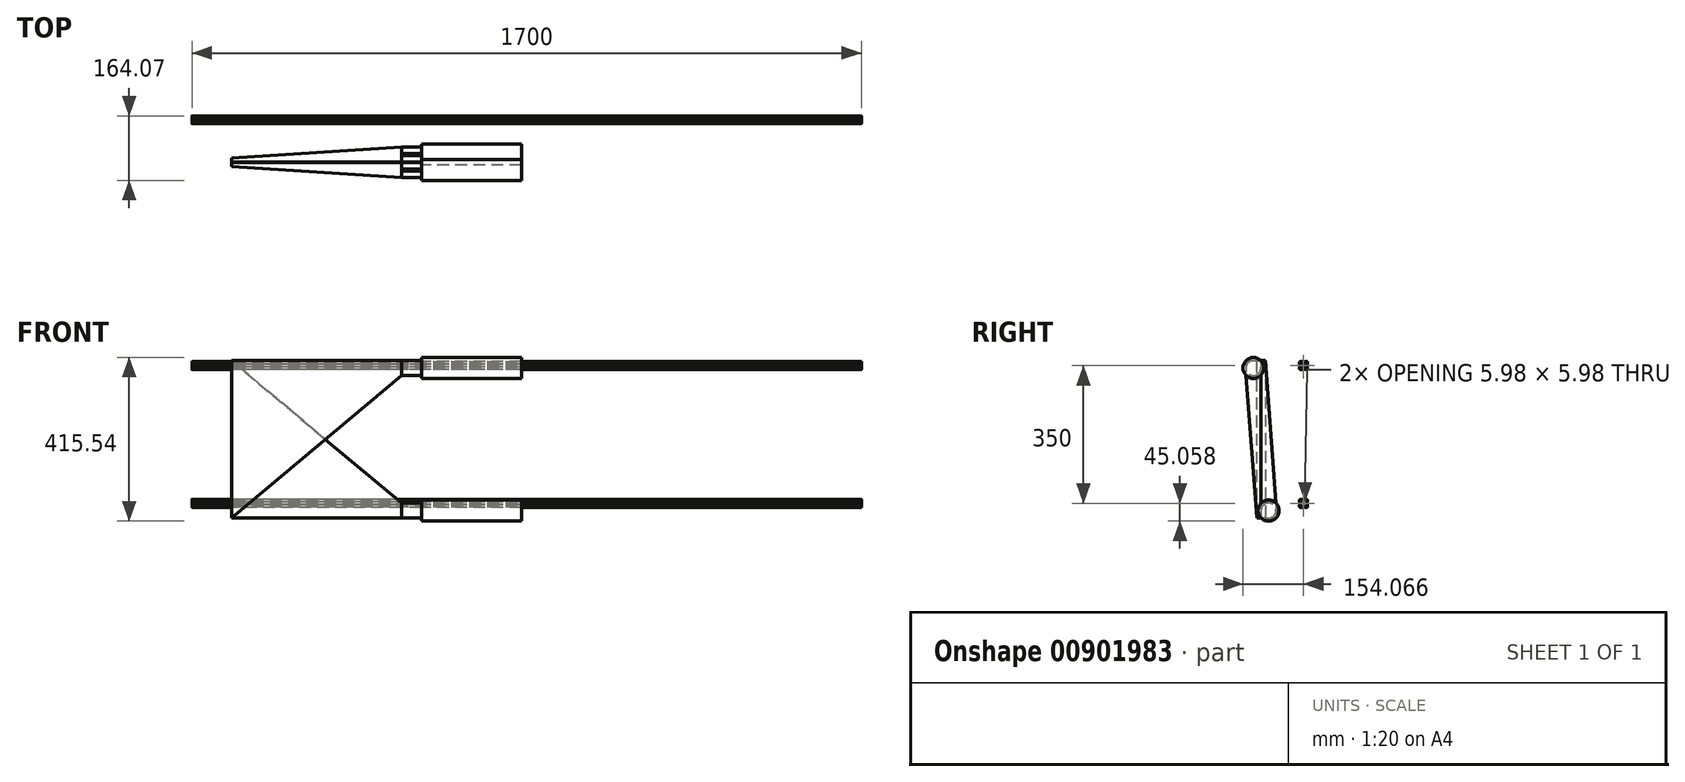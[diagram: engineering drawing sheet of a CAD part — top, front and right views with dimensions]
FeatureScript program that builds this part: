
annotation { "Feature Type Name" : "Feature", "Feature Type Description" : "" }
export const myFeature = defineFeature(function(context is Context, id is Id, definition is map)
    precondition{}
    {
        {
            var Q0;
            Q0=qCreatedBy(makeId("Right.planeOp"),FACE);
            var sketch = newSketch(context, id + "F0", { "sketchPlane" : qUnion([Q0])});
            skLineSegment(sketch, "E0.bottom", {"start": v(0, 324.79) * mm, "end": v(38.1, 324.79) * mm});
            skLineSegment(sketch, "E0.top", {"start": v(0, -75.21) * mm, "end": v(38.1, -75.21) * mm});
            skLineSegment(sketch, "E0.left", {"start": v(0, 324.79) * mm, "end": v(0, -75.21) * mm});
            skLineSegment(sketch, "E0.right", {"start": v(38.1, 324.79) * mm, "end": v(38.1, -75.21) * mm});
            skLineSegment(sketch, "E1.bottom", {"start": v(-38.6, 324.79) * mm, "end": v(-0.5, 324.79) * mm});
            skLineSegment(sketch, "E1.top", {"start": v(-38.6, -75.21) * mm, "end": v(-0.5, -75.21) * mm});
            skLineSegment(sketch, "E1.left", {"start": v(-38.6, 324.79) * mm, "end": v(-38.6, -75.21) * mm});
            skLineSegment(sketch, "E1.right", {"start": v(-0.5, 324.79) * mm, "end": v(-0.5, -75.21) * mm});
            skSolve(sketch);
        }
        {
            var Q0;
            Q0=makeQuery(id+"F0.imprint","IMPRINT",FACE,{"disambiguationData":[TD([[makeQuery(id+"F0.imprint","IMPRINT",EDGE,{"derivedFrom":sQuery(id+"F0.wireOp",EDGE,"E1.bottom")}),-1.0]])]});
            var Q1;
            Q1=makeQuery(id+"F0.imprint","IMPRINT",FACE,{"disambiguationData":[TD([[makeQuery(id+"F0.imprint","IMPRINT",EDGE,{"derivedFrom":sQuery(id+"F0.wireOp",EDGE,"E0.bottom")}),-1.0]])]});
            extrude(context, id + "F1", {"entities" : qUnion([Q0, Q1]), "depth" : 431.8 * mm, "offsetDistance" : 25 * mm});
        }
        {
            var Q0;
            Q0=makeQuery(id+"F1.opExtrude","CAP_EDGE",EDGE,{"disambiguationData":[OSD([sQuery(id+"F0.wireOp",EDGE,"E0.right")])],"isStart":true});
            chamfer(context, id + "F2", {"entities" : qUnion([Q0]), "chamferType" : ChamferType.TWO_OFFSETS, "width1" : 27.8 * mm, "oppositeDirection" : false, "width2" : 431.8 * mm, "tangentPropagation" : true});
        }
        {
            var Q0;
            Q0=makeQuery(id+"F1.opExtrude","CAP_EDGE",EDGE,{"disambiguationData":[OSD([sQuery(id+"F0.wireOp",EDGE,"E1.left")])],"isStart":true});
            chamfer(context, id + "F3", {"entities" : qUnion([Q0]), "chamferType" : ChamferType.TWO_OFFSETS, "width1" : 431.8 * mm, "oppositeDirection" : false, "width2" : 27.8 * mm, "tangentPropagation" : true});
        }
        {
            var Q0;
            Q0=makeQuery(id+"F1.opExtrude","CAP_EDGE",EDGE,{"disambiguationData":[OSD([sQuery(id+"F0.wireOp",EDGE,"E0.bottom")])],"isStart":false});
            chamfer(context, id + "F4", {"entities" : qUnion([Q0]), "chamferType" : ChamferType.TWO_OFFSETS, "width1" : 431.8 * mm, "oppositeDirection" : false, "width2" : 362.2 * mm, "tangentPropagation" : true});
        }
        {
            var Q0;
            Q0=makeQuery(id+"F1.opExtrude","CAP_EDGE",EDGE,{"disambiguationData":[OSD([sQuery(id+"F0.wireOp",EDGE,"E1.top")])],"isStart":false});
            chamfer(context, id + "F5", {"entities" : qUnion([Q0]), "chamferType" : ChamferType.TWO_OFFSETS, "width1" : 362.2 * mm, "oppositeDirection" : false, "width2" : 431.8 * mm, "tangentPropagation" : true});
        }
        {
            var Q0;
            Q0=makeQuery(id+"F1.opExtrude","CAP_FACE",FACE,{"disambiguationData":[OSD([sQuery(id+"F0.wireOp",EDGE,"E0.bottom"),sQuery(id+"F0.wireOp",EDGE,"E0.top"),sQuery(id+"F0.wireOp",EDGE,"E0.left"),sQuery(id+"F0.wireOp",EDGE,"E0.right")])],"isStart":false});
            var sketch = newSketch(context, id + "F6", { "sketchPlane" : qUnion([Q0])});
            skCircle(sketch, "E2", {"center": v(19.05, -56.31) * mm, "radius": 19.05 * mm});
            skSolve(sketch);
        }
        {
            var Q0;
            Q0=makeQuery(id+"F1.opExtrude","CAP_FACE",FACE,{"disambiguationData":[OSD([sQuery(id+"F0.wireOp",EDGE,"E1.bottom"),sQuery(id+"F0.wireOp",EDGE,"E1.top"),sQuery(id+"F0.wireOp",EDGE,"E1.left"),sQuery(id+"F0.wireOp",EDGE,"E1.right")])],"isStart":false});
            var sketch = newSketch(context, id + "F7", { "sketchPlane" : qUnion([Q0])});
            skCircle(sketch, "E3", {"center": v(-19.56, 305.89) * mm, "radius": 19.05 * mm});
            skSolve(sketch);
        }
        {
            var Q0;
            {var subQ0=sQuery(id+"F6.wireOp",EDGE,"E2");var subQ1=sQuery(id+"F0.wireOp",EDGE,"E0.left");var subQ2=makeQuery(id+"F6.imprint","INTERSECT",VERTEX,{"derivedFrom":[makeQuery(id+"F1.opExtrude","CAP_EDGE",EDGE,{"disambiguationData":[OSD([subQ1])],"isStart":false}),subQ0]});Q0=makeQuery(id+"F6.imprint","IMPRINT",FACE,{"disambiguationData":[TD([[makeQuery(id+"F6.imprint","IMPRINT",EDGE,{"disambiguationData":[TD([[subQ2,-1.0]])],"derivedFrom":subQ0}),1.0]])]});}
            var Q1;
            {var subQ0=sQuery(id+"F7.wireOp",EDGE,"E3");var subQ4=sQuery(id+"F0.wireOp",EDGE,"E1.bottom");var subQ9=makeQuery(id+"F1.opExtrude","CAP_EDGE",EDGE,{"disambiguationData":[OSD([subQ4])],"isStart":false});var subQ13=makeQuery(id+"F7.imprint","INTERSECT",VERTEX,{"disambiguationData":[OD(0.0)],"derivedFrom":[subQ9,subQ0]});Q1=makeQuery(id+"F7.imprint","IMPRINT",FACE,{"disambiguationData":[TD([[makeQuery(id+"F7.imprint","IMPRINT",EDGE,{"disambiguationData":[TD([[subQ13,1.0]])],"derivedFrom":subQ0}),1.0]])]});}
            extrude(context, id + "F8", {"entities" : qUnion([Q0, Q1]), "depth" : 50.8 * mm, "offsetDistance" : 25 * mm, "hasSecondDirection" : true, "secondDirectionOppositeDirection" : false, "secondDirectionDepth" : 0.01 * mm});
        }
        {
            var Q0;
            Q0=makeQuery(id+"F8.opExtrude","CAP_FACE",FACE,{"disambiguationData":[OSD([sQuery(id+"F0.wireOp",EDGE,"E1.bottom"),sQuery(id+"F0.wireOp",EDGE,"E1.top"),sQuery(id+"F0.wireOp",EDGE,"E1.left"),sQuery(id+"F0.wireOp",EDGE,"E1.right"),sQuery(id+"F7.wireOp",EDGE,"E3")])],"isStart":false});
            var sketch = newSketch(context, id + "F9", { "sketchPlane" : qUnion([Q0])});
            skCircle(sketch, "E4", {"center": v(-19.56, 305.89) * mm, "radius": 26.67 * mm});
            skSolve(sketch);
        }
        {
            var Q0;
            Q0=makeQuery(id+"F8.opExtrude","CAP_FACE",FACE,{"disambiguationData":[OSD([sQuery(id+"F0.wireOp",EDGE,"E0.bottom"),sQuery(id+"F0.wireOp",EDGE,"E0.top"),sQuery(id+"F0.wireOp",EDGE,"E0.left"),sQuery(id+"F0.wireOp",EDGE,"E0.right"),sQuery(id+"F6.wireOp",EDGE,"E2")])],"isStart":false});
            var sketch = newSketch(context, id + "F10", { "sketchPlane" : qUnion([Q0])});
            skCircle(sketch, "E5", {"center": v(19.05, -56.31) * mm, "radius": 26.67 * mm});
            skSolve(sketch);
        }
        {
            var Q0;
            {var subQ5=sQuery(id+"F0.wireOp",EDGE,"E1.bottom");Q0=makeQuery(id+"F9.imprint","IMPRINT",FACE,{"disambiguationData":[TD([[makeQuery(id+"F9.imprint","IMPRINT",EDGE,{"derivedFrom":makeQuery(id+"F8.opExtrude","CAP_EDGE",EDGE,{"disambiguationData":[OSD([subQ5])],"isStart":false})}),-1.0]])]});}
            var Q1;
            Q1=makeQuery(id+"F9.imprint","IMPRINT",FACE,{"disambiguationData":[TD([[makeQuery(id+"F9.imprint","IMPRINT",EDGE,{"derivedFrom":sQuery(id+"F9.wireOp",EDGE,"E4")}),1.0]])]});
            var Q2;
            {var subQ3=sQuery(id+"F0.wireOp",EDGE,"E0.top");Q2=makeQuery(id+"F10.imprint","IMPRINT",FACE,{"disambiguationData":[TD([[makeQuery(id+"F10.imprint","IMPRINT",EDGE,{"derivedFrom":makeQuery(id+"F8.opExtrude","CAP_EDGE",EDGE,{"disambiguationData":[OSD([subQ3])],"isStart":false})}),1.0]])]});}
            var Q3;
            Q3=makeQuery(id+"F10.imprint","IMPRINT",FACE,{"disambiguationData":[TD([[makeQuery(id+"F10.imprint","IMPRINT",EDGE,{"derivedFrom":sQuery(id+"F10.wireOp",EDGE,"E5")}),1.0]])]});
            extrude(context, id + "F11", {"entities" : qUnion([Q0, Q1, Q2, Q3]), "depth" : 254 * mm, "offsetDistance" : 25 * mm, "hasSecondDirection" : true, "secondDirectionOppositeDirection" : false, "secondDirectionDepth" : 0.01 * mm});
        }
        {
            var Q0;
            Q0=qCreatedBy(makeId("Right.planeOp"),FACE);
            var sketch = newSketch(context, id + "F12", { "sketchPlane" : qUnion([Q0])});
            skArc(sketch, "E6", {"start": v(79.34, 322.08) * mm, "mid": v(78.28, 321.64) * mm, "end": v(77.84, 320.58) * mm});
            skLineSegment(sketch, "E7", {"start": v(77.84, 320.58) * mm, "end": v(77.84, 315.83) * mm});
            skArc(sketch, "E8", {"start": v(77.84, 315.83) * mm, "mid": v(77.9, 315.69) * mm, "end": v(78.04, 315.63) * mm});
            skLineSegment(sketch, "E9", {"start": v(78.04, 315.63) * mm, "end": v(78.14, 315.63) * mm});
            skArc(sketch, "E10", {"start": v(78.34, 315.43) * mm, "mid": v(78.28, 315.57) * mm, "end": v(78.14, 315.63) * mm});
            skLineSegment(sketch, "E11", {"start": v(78.34, 315.43) * mm, "end": v(78.34, 315.28) * mm});
            skArc(sketch, "E12", {"start": v(78.34, 315.28) * mm, "mid": v(78.4, 315.14) * mm, "end": v(78.54, 315.08) * mm});
            skLineSegment(sketch, "E13", {"start": v(78.54, 315.08) * mm, "end": v(78.84, 315.08) * mm});
            skArc(sketch, "E14", {"start": v(78.84, 315.08) * mm, "mid": v(79.2, 315.22) * mm, "end": v(79.34, 315.58) * mm});
            skLineSegment(sketch, "E15", {"start": v(79.34, 315.58) * mm, "end": v(79.34, 317.58) * mm});
            skArc(sketch, "E16", {"start": v(79.84, 318.08) * mm, "mid": v(79.48, 317.93) * mm, "end": v(79.34, 317.58) * mm});
            skLineSegment(sketch, "E17", {"start": v(79.84, 318.08) * mm, "end": v(80.57, 318.08) * mm});
            skArc(sketch, "E18", {"start": v(80.92, 317.93) * mm, "mid": v(80.76, 318.04) * mm, "end": v(80.57, 318.08) * mm});
            skLineSegment(sketch, "E19", {"start": v(80.92, 317.93) * mm, "end": v(83.2, 315.66) * mm});
            skArc(sketch, "E20", {"start": v(83.34, 315.3) * mm, "mid": v(83.3, 315.5) * mm, "end": v(83.2, 315.66) * mm});
            skLineSegment(sketch, "E21", {"start": v(83.34, 315.3) * mm, "end": v(83.34, 313.03) * mm});
            skArc(sketch, "E22", {"start": v(83.34, 313.03) * mm, "mid": v(83.34, 312.98) * mm, "end": v(83.36, 312.93) * mm});
            skLineSegment(sketch, "E23", {"start": v(83.36, 312.93) * mm, "end": v(83.8, 312.18) * mm});
            skArc(sketch, "E24", {"start": v(83.8, 311.98) * mm, "mid": v(83.83, 312.08) * mm, "end": v(83.8, 312.18) * mm});
            skLineSegment(sketch, "E25", {"start": v(83.8, 311.98) * mm, "end": v(83.36, 311.22) * mm});
            skArc(sketch, "E26", {"start": v(83.36, 311.22) * mm, "mid": v(83.34, 311.18) * mm, "end": v(83.34, 311.12) * mm});
            skLineSegment(sketch, "E27", {"start": v(83.34, 311.12) * mm, "end": v(83.34, 308.85) * mm});
            skArc(sketch, "E28", {"start": v(83.2, 308.5) * mm, "mid": v(83.3, 308.65) * mm, "end": v(83.34, 308.85) * mm});
            skLineSegment(sketch, "E29", {"start": v(83.2, 308.5) * mm, "end": v(80.92, 306.22) * mm});
            skArc(sketch, "E30", {"start": v(80.57, 306.08) * mm, "mid": v(80.76, 306.12) * mm, "end": v(80.92, 306.22) * mm});
            skLineSegment(sketch, "E31", {"start": v(80.57, 306.08) * mm, "end": v(79.84, 306.08) * mm});
            skArc(sketch, "E32", {"start": v(79.34, 306.58) * mm, "mid": v(79.48, 306.22) * mm, "end": v(79.84, 306.08) * mm});
            skLineSegment(sketch, "E33", {"start": v(79.34, 306.58) * mm, "end": v(79.34, 308.58) * mm});
            skArc(sketch, "E34", {"start": v(79.34, 308.58) * mm, "mid": v(79.2, 308.93) * mm, "end": v(78.84, 309.08) * mm});
            skLineSegment(sketch, "E35", {"start": v(78.84, 309.08) * mm, "end": v(78.54, 309.08) * mm});
            skArc(sketch, "E36", {"start": v(78.54, 309.08) * mm, "mid": v(78.4, 309.02) * mm, "end": v(78.34, 308.88) * mm});
            skLineSegment(sketch, "E37", {"start": v(78.34, 308.88) * mm, "end": v(78.34, 308.73) * mm});
            skArc(sketch, "E38", {"start": v(78.14, 308.53) * mm, "mid": v(78.28, 308.59) * mm, "end": v(78.34, 308.73) * mm});
            skLineSegment(sketch, "E39", {"start": v(78.14, 308.53) * mm, "end": v(78.04, 308.53) * mm});
            skArc(sketch, "E40", {"start": v(78.04, 308.53) * mm, "mid": v(77.9, 308.47) * mm, "end": v(77.84, 308.33) * mm});
            skLineSegment(sketch, "E41", {"start": v(77.84, 308.33) * mm, "end": v(77.84, 303.58) * mm});
            skArc(sketch, "E42", {"start": v(77.84, 303.58) * mm, "mid": v(78.28, 302.52) * mm, "end": v(79.34, 302.08) * mm});
            skLineSegment(sketch, "E43", {"start": v(79.34, 302.08) * mm, "end": v(84.09, 302.08) * mm});
            skArc(sketch, "E44", {"start": v(84.09, 302.08) * mm, "mid": v(84.23, 302.14) * mm, "end": v(84.29, 302.28) * mm});
            skLineSegment(sketch, "E45", {"start": v(84.29, 302.28) * mm, "end": v(84.29, 302.38) * mm});
            skArc(sketch, "E46", {"start": v(84.49, 302.58) * mm, "mid": v(84.35, 302.52) * mm, "end": v(84.29, 302.38) * mm});
            skLineSegment(sketch, "E47", {"start": v(84.49, 302.58) * mm, "end": v(84.64, 302.58) * mm});
            skArc(sketch, "E48", {"start": v(84.64, 302.58) * mm, "mid": v(84.78, 302.64) * mm, "end": v(84.84, 302.78) * mm});
            skLineSegment(sketch, "E49", {"start": v(84.84, 302.78) * mm, "end": v(84.84, 303.08) * mm});
            skArc(sketch, "E50", {"start": v(84.84, 303.08) * mm, "mid": v(84.7, 303.43) * mm, "end": v(84.34, 303.58) * mm});
            skLineSegment(sketch, "E51", {"start": v(84.34, 303.58) * mm, "end": v(82.34, 303.58) * mm});
            skArc(sketch, "E52", {"start": v(81.84, 304.08) * mm, "mid": v(81.98, 303.72) * mm, "end": v(82.34, 303.58) * mm});
            skLineSegment(sketch, "E53", {"start": v(81.84, 304.08) * mm, "end": v(81.84, 304.8) * mm});
            skArc(sketch, "E54", {"start": v(81.98, 305.16) * mm, "mid": v(81.87, 305) * mm, "end": v(81.84, 304.8) * mm});
            skLineSegment(sketch, "E55", {"start": v(81.98, 305.16) * mm, "end": v(84.25, 307.43) * mm});
            skArc(sketch, "E56", {"start": v(84.6, 307.58) * mm, "mid": v(84.41, 307.54) * mm, "end": v(84.25, 307.43) * mm});
            skLineSegment(sketch, "E57", {"start": v(84.6, 307.58) * mm, "end": v(86.88, 307.58) * mm});
            skArc(sketch, "E58", {"start": v(86.88, 307.58) * mm, "mid": v(86.93, 307.58) * mm, "end": v(86.98, 307.6) * mm});
            skLineSegment(sketch, "E59", {"start": v(86.98, 307.6) * mm, "end": v(87.74, 308.04) * mm});
            skArc(sketch, "E60", {"start": v(87.94, 308.04) * mm, "mid": v(87.84, 308.07) * mm, "end": v(87.74, 308.04) * mm});
            skLineSegment(sketch, "E61", {"start": v(87.94, 308.04) * mm, "end": v(88.7, 307.6) * mm});
            skArc(sketch, "E62", {"start": v(88.7, 307.6) * mm, "mid": v(88.74, 307.58) * mm, "end": v(88.8, 307.58) * mm});
            skLineSegment(sketch, "E63", {"start": v(88.8, 307.58) * mm, "end": v(91.07, 307.58) * mm});
            skArc(sketch, "E64", {"start": v(91.42, 307.43) * mm, "mid": v(91.26, 307.54) * mm, "end": v(91.07, 307.58) * mm});
            skLineSegment(sketch, "E65", {"start": v(91.42, 307.43) * mm, "end": v(93.7, 305.16) * mm});
            skArc(sketch, "E66", {"start": v(93.84, 304.8) * mm, "mid": v(93.8, 305) * mm, "end": v(93.7, 305.16) * mm});
            skLineSegment(sketch, "E67", {"start": v(93.84, 304.8) * mm, "end": v(93.84, 304.08) * mm});
            skArc(sketch, "E68", {"start": v(93.34, 303.58) * mm, "mid": v(93.7, 303.72) * mm, "end": v(93.84, 304.08) * mm});
            skLineSegment(sketch, "E69", {"start": v(93.34, 303.58) * mm, "end": v(91.34, 303.58) * mm});
            skArc(sketch, "E70", {"start": v(91.34, 303.58) * mm, "mid": v(90.98, 303.43) * mm, "end": v(90.84, 303.08) * mm});
            skLineSegment(sketch, "E71", {"start": v(90.84, 303.08) * mm, "end": v(90.84, 302.78) * mm});
            skArc(sketch, "E72", {"start": v(90.84, 302.78) * mm, "mid": v(90.9, 302.64) * mm, "end": v(91.04, 302.58) * mm});
            skLineSegment(sketch, "E73", {"start": v(91.04, 302.58) * mm, "end": v(91.19, 302.58) * mm});
            skArc(sketch, "E74", {"start": v(91.39, 302.38) * mm, "mid": v(91.33, 302.52) * mm, "end": v(91.19, 302.58) * mm});
            skLineSegment(sketch, "E75", {"start": v(91.39, 302.38) * mm, "end": v(91.39, 302.28) * mm});
            skArc(sketch, "E76", {"start": v(91.39, 302.28) * mm, "mid": v(91.45, 302.14) * mm, "end": v(91.59, 302.08) * mm});
            skLineSegment(sketch, "E77", {"start": v(91.59, 302.08) * mm, "end": v(96.34, 302.08) * mm});
            skArc(sketch, "E78", {"start": v(96.34, 302.08) * mm, "mid": v(97.4, 302.52) * mm, "end": v(97.84, 303.58) * mm});
            skLineSegment(sketch, "E79", {"start": v(97.84, 303.58) * mm, "end": v(97.84, 308.33) * mm});
            skArc(sketch, "E80", {"start": v(97.84, 308.33) * mm, "mid": v(97.78, 308.47) * mm, "end": v(97.64, 308.53) * mm});
            skLineSegment(sketch, "E81", {"start": v(97.64, 308.53) * mm, "end": v(97.54, 308.53) * mm});
            skArc(sketch, "E82", {"start": v(97.34, 308.73) * mm, "mid": v(97.4, 308.59) * mm, "end": v(97.54, 308.53) * mm});
            skLineSegment(sketch, "E83", {"start": v(97.34, 308.73) * mm, "end": v(97.34, 308.88) * mm});
            skArc(sketch, "E84", {"start": v(97.34, 308.88) * mm, "mid": v(97.28, 309.02) * mm, "end": v(97.14, 309.08) * mm});
            skLineSegment(sketch, "E85", {"start": v(97.14, 309.08) * mm, "end": v(96.84, 309.08) * mm});
            skArc(sketch, "E86", {"start": v(96.84, 309.08) * mm, "mid": v(96.48, 308.93) * mm, "end": v(96.34, 308.58) * mm});
            skLineSegment(sketch, "E87", {"start": v(96.34, 308.58) * mm, "end": v(96.34, 306.58) * mm});
            skArc(sketch, "E88", {"start": v(95.84, 306.08) * mm, "mid": v(96.2, 306.22) * mm, "end": v(96.34, 306.58) * mm});
            skLineSegment(sketch, "E89", {"start": v(95.84, 306.08) * mm, "end": v(95.1, 306.08) * mm});
            skArc(sketch, "E90", {"start": v(94.75, 306.22) * mm, "mid": v(94.91, 306.12) * mm, "end": v(95.1, 306.08) * mm});
            skLineSegment(sketch, "E91", {"start": v(94.75, 306.22) * mm, "end": v(92.48, 308.5) * mm});
            skArc(sketch, "E92", {"start": v(92.34, 308.85) * mm, "mid": v(92.37, 308.65) * mm, "end": v(92.48, 308.5) * mm});
            skLineSegment(sketch, "E93", {"start": v(92.34, 308.85) * mm, "end": v(92.34, 311.12) * mm});
            skArc(sketch, "E94", {"start": v(92.34, 311.12) * mm, "mid": v(92.33, 311.18) * mm, "end": v(92.3, 311.22) * mm});
            skLineSegment(sketch, "E95", {"start": v(92.3, 311.22) * mm, "end": v(91.87, 311.98) * mm});
            skArc(sketch, "E96", {"start": v(91.87, 312.18) * mm, "mid": v(91.85, 312.08) * mm, "end": v(91.87, 311.98) * mm});
            skLineSegment(sketch, "E97", {"start": v(91.87, 312.18) * mm, "end": v(92.3, 312.93) * mm});
            skArc(sketch, "E98", {"start": v(92.3, 312.93) * mm, "mid": v(92.33, 312.98) * mm, "end": v(92.34, 313.03) * mm});
            skLineSegment(sketch, "E99", {"start": v(92.34, 313.03) * mm, "end": v(92.34, 315.3) * mm});
            skArc(sketch, "E100", {"start": v(92.48, 315.66) * mm, "mid": v(92.37, 315.5) * mm, "end": v(92.34, 315.3) * mm});
            skLineSegment(sketch, "E101", {"start": v(92.48, 315.66) * mm, "end": v(94.75, 317.93) * mm});
            skArc(sketch, "E102", {"start": v(95.1, 318.08) * mm, "mid": v(94.91, 318.04) * mm, "end": v(94.75, 317.93) * mm});
            skLineSegment(sketch, "E103", {"start": v(95.1, 318.08) * mm, "end": v(95.84, 318.08) * mm});
            skArc(sketch, "E104", {"start": v(96.34, 317.58) * mm, "mid": v(96.2, 317.93) * mm, "end": v(95.84, 318.08) * mm});
            skLineSegment(sketch, "E105", {"start": v(96.34, 317.58) * mm, "end": v(96.34, 315.58) * mm});
            skArc(sketch, "E106", {"start": v(96.34, 315.58) * mm, "mid": v(96.48, 315.22) * mm, "end": v(96.84, 315.08) * mm});
            skLineSegment(sketch, "E107", {"start": v(96.84, 315.08) * mm, "end": v(97.14, 315.08) * mm});
            skArc(sketch, "E108", {"start": v(97.14, 315.08) * mm, "mid": v(97.28, 315.14) * mm, "end": v(97.34, 315.28) * mm});
            skLineSegment(sketch, "E109", {"start": v(97.34, 315.28) * mm, "end": v(97.34, 315.43) * mm});
            skArc(sketch, "E110", {"start": v(97.54, 315.63) * mm, "mid": v(97.4, 315.57) * mm, "end": v(97.34, 315.43) * mm});
            skLineSegment(sketch, "E111", {"start": v(97.54, 315.63) * mm, "end": v(97.64, 315.63) * mm});
            skArc(sketch, "E112", {"start": v(97.64, 315.63) * mm, "mid": v(97.78, 315.69) * mm, "end": v(97.84, 315.83) * mm});
            skLineSegment(sketch, "E113", {"start": v(97.84, 315.83) * mm, "end": v(97.84, 320.58) * mm});
            skArc(sketch, "E114", {"start": v(97.84, 320.58) * mm, "mid": v(97.4, 321.64) * mm, "end": v(96.34, 322.08) * mm});
            skLineSegment(sketch, "E115", {"start": v(96.34, 322.08) * mm, "end": v(91.59, 322.08) * mm});
            skArc(sketch, "E116", {"start": v(91.59, 322.08) * mm, "mid": v(91.45, 322.02) * mm, "end": v(91.39, 321.88) * mm});
            skLineSegment(sketch, "E117", {"start": v(91.39, 321.88) * mm, "end": v(91.39, 321.78) * mm});
            skArc(sketch, "E118", {"start": v(91.19, 321.58) * mm, "mid": v(91.33, 321.64) * mm, "end": v(91.39, 321.78) * mm});
            skLineSegment(sketch, "E119", {"start": v(91.19, 321.58) * mm, "end": v(91.04, 321.58) * mm});
            skArc(sketch, "E120", {"start": v(91.04, 321.58) * mm, "mid": v(90.9, 321.52) * mm, "end": v(90.84, 321.38) * mm});
            skLineSegment(sketch, "E121", {"start": v(90.84, 321.38) * mm, "end": v(90.84, 321.08) * mm});
            skArc(sketch, "E122", {"start": v(90.84, 321.08) * mm, "mid": v(90.98, 320.72) * mm, "end": v(91.34, 320.58) * mm});
            skLineSegment(sketch, "E123", {"start": v(91.34, 320.58) * mm, "end": v(93.34, 320.58) * mm});
            skArc(sketch, "E124", {"start": v(93.84, 320.08) * mm, "mid": v(93.7, 320.43) * mm, "end": v(93.34, 320.58) * mm});
            skLineSegment(sketch, "E125", {"start": v(93.84, 320.08) * mm, "end": v(93.84, 319.35) * mm});
            skArc(sketch, "E126", {"start": v(93.7, 319) * mm, "mid": v(93.8, 319.15) * mm, "end": v(93.84, 319.35) * mm});
            skLineSegment(sketch, "E127", {"start": v(93.7, 319) * mm, "end": v(91.42, 316.72) * mm});
            skArc(sketch, "E128", {"start": v(91.07, 316.58) * mm, "mid": v(91.26, 316.62) * mm, "end": v(91.42, 316.72) * mm});
            skLineSegment(sketch, "E129", {"start": v(91.07, 316.58) * mm, "end": v(88.8, 316.58) * mm});
            skArc(sketch, "E130", {"start": v(88.8, 316.58) * mm, "mid": v(88.74, 316.57) * mm, "end": v(88.7, 316.55) * mm});
            skLineSegment(sketch, "E131", {"start": v(88.7, 316.55) * mm, "end": v(87.94, 316.12) * mm});
            skArc(sketch, "E132", {"start": v(87.74, 316.12) * mm, "mid": v(87.84, 316.09) * mm, "end": v(87.94, 316.12) * mm});
            skLineSegment(sketch, "E133", {"start": v(87.74, 316.12) * mm, "end": v(86.98, 316.55) * mm});
            skArc(sketch, "E134", {"start": v(86.98, 316.55) * mm, "mid": v(86.93, 316.57) * mm, "end": v(86.88, 316.58) * mm});
            skLineSegment(sketch, "E135", {"start": v(86.88, 316.58) * mm, "end": v(84.6, 316.58) * mm});
            skArc(sketch, "E136", {"start": v(84.25, 316.72) * mm, "mid": v(84.41, 316.62) * mm, "end": v(84.6, 316.58) * mm});
            skLineSegment(sketch, "E137", {"start": v(84.25, 316.72) * mm, "end": v(81.98, 319) * mm});
            skArc(sketch, "E138", {"start": v(81.84, 319.35) * mm, "mid": v(81.87, 319.15) * mm, "end": v(81.98, 319) * mm});
            skLineSegment(sketch, "E139", {"start": v(81.84, 319.35) * mm, "end": v(81.84, 320.08) * mm});
            skArc(sketch, "E140", {"start": v(82.34, 320.58) * mm, "mid": v(81.98, 320.43) * mm, "end": v(81.84, 320.08) * mm});
            skLineSegment(sketch, "E141", {"start": v(82.34, 320.58) * mm, "end": v(84.34, 320.58) * mm});
            skArc(sketch, "E142", {"start": v(84.34, 320.58) * mm, "mid": v(84.7, 320.72) * mm, "end": v(84.84, 321.08) * mm});
            skLineSegment(sketch, "E143", {"start": v(84.84, 321.08) * mm, "end": v(84.84, 321.38) * mm});
            skArc(sketch, "E144", {"start": v(84.84, 321.38) * mm, "mid": v(84.78, 321.52) * mm, "end": v(84.64, 321.58) * mm});
            skLineSegment(sketch, "E145", {"start": v(84.64, 321.58) * mm, "end": v(84.49, 321.58) * mm});
            skArc(sketch, "E146", {"start": v(84.29, 321.78) * mm, "mid": v(84.35, 321.64) * mm, "end": v(84.49, 321.58) * mm});
            skLineSegment(sketch, "E147", {"start": v(84.29, 321.78) * mm, "end": v(84.29, 321.88) * mm});
            skArc(sketch, "E148", {"start": v(84.29, 321.88) * mm, "mid": v(84.23, 322.02) * mm, "end": v(84.09, 322.08) * mm});
            skLineSegment(sketch, "E149", {"start": v(84.09, 322.08) * mm, "end": v(79.34, 322.08) * mm});
            skArc(sketch, "E150", {"start": v(85.92, 315.07) * mm, "mid": v(85.32, 314.59) * mm, "end": v(84.84, 313.99) * mm});
            skLineSegment(sketch, "E151", {"start": v(86.58, 314.52) * mm, "end": v(85.92, 315.07) * mm});
            skArc(sketch, "E152", {"start": v(89.1, 314.52) * mm, "mid": v(87.84, 314.83) * mm, "end": v(86.58, 314.52) * mm});
            skLineSegment(sketch, "E153", {"start": v(89.75, 315.07) * mm, "end": v(89.1, 314.52) * mm});
            skArc(sketch, "E154", {"start": v(90.83, 313.99) * mm, "mid": v(90.35, 314.59) * mm, "end": v(89.75, 315.07) * mm});
            skLineSegment(sketch, "E155", {"start": v(90.28, 313.34) * mm, "end": v(90.83, 313.99) * mm});
            skArc(sketch, "E156", {"start": v(90.28, 310.82) * mm, "mid": v(90.59, 312.08) * mm, "end": v(90.28, 313.34) * mm});
            skLineSegment(sketch, "E157", {"start": v(90.83, 310.17) * mm, "end": v(90.28, 310.82) * mm});
            skArc(sketch, "E158", {"start": v(89.75, 309.09) * mm, "mid": v(90.35, 309.57) * mm, "end": v(90.83, 310.17) * mm});
            skLineSegment(sketch, "E159", {"start": v(89.1, 309.63) * mm, "end": v(89.75, 309.09) * mm});
            skArc(sketch, "E160", {"start": v(86.58, 309.63) * mm, "mid": v(87.84, 309.33) * mm, "end": v(89.1, 309.63) * mm});
            skLineSegment(sketch, "E161", {"start": v(85.92, 309.09) * mm, "end": v(86.58, 309.63) * mm});
            skArc(sketch, "E162", {"start": v(84.84, 310.17) * mm, "mid": v(85.32, 309.57) * mm, "end": v(85.92, 309.09) * mm});
            skLineSegment(sketch, "E163", {"start": v(85.4, 310.82) * mm, "end": v(84.84, 310.17) * mm});
            skArc(sketch, "E164", {"start": v(85.4, 313.34) * mm, "mid": v(85.09, 312.08) * mm, "end": v(85.4, 310.82) * mm});
            skLineSegment(sketch, "E165", {"start": v(84.84, 313.99) * mm, "end": v(85.4, 313.34) * mm});
            skSolve(sketch);
        }
        {
            var Q0;
            Q0=makeQuery(id+"F12.imprint","IMPRINT",FACE,{"disambiguationData":[TD([[makeQuery(id+"F12.imprint","IMPRINT",EDGE,{"derivedFrom":sQuery(id+"F12.wireOp",EDGE,"E6")}),1.0]])]});
            var Q1;
            Q1=sQuery(id+"F12.wireOp",EDGE,"E41");
            var Q2;
            Q2=sQuery(id+"F12.wireOp",EDGE,"E43");
            var Q3;
            Q3=sQuery(id+"F12.wireOp",EDGE,"E79");
            var Q4;
            Q4=sQuery(id+"F12.wireOp",EDGE,"E114");
            var Q5;
            Q5=sQuery(id+"F12.wireOp",EDGE,"E113");
            var Q6;
            Q6=sQuery(id+"F12.wireOp",EDGE,"E7");
            var Q7;
            Q7=sQuery(id+"F12.wireOp",EDGE,"E115");
            var Q8;
            Q8=sQuery(id+"F12.wireOp",EDGE,"E104");
            var Q9;
            Q9=sQuery(id+"F12.wireOp",EDGE,"E77");
            var Q10;
            Q10=sQuery(id+"F12.wireOp",EDGE,"E125");
            var Q11;
            Q11=sQuery(id+"F12.wireOp",EDGE,"E93");
            var Q12;
            Q12=sQuery(id+"F12.wireOp",EDGE,"E124");
            var Q13;
            Q13=sQuery(id+"F12.wireOp",EDGE,"E102");
            var Q14;
            Q14=sQuery(id+"F12.wireOp",EDGE,"E126");
            var Q15;
            Q15=sQuery(id+"F12.wireOp",EDGE,"E103");
            var Q16;
            Q16=sQuery(id+"F12.wireOp",EDGE,"E65");
            var Q17;
            Q17=sQuery(id+"F12.wireOp",EDGE,"E55");
            var Q18;
            Q18=sQuery(id+"F12.wireOp",EDGE,"E92");
            var Q19;
            Q19=sQuery(id+"F12.wireOp",EDGE,"E91");
            var Q20;
            Q20=sQuery(id+"F12.wireOp",EDGE,"E127");
            var Q21;
            Q21=sQuery(id+"F12.wireOp",EDGE,"E101");
            var Q22;
            Q22=sQuery(id+"F12.wireOp",EDGE,"E53");
            var Q23;
            Q23=sQuery(id+"F12.wireOp",EDGE,"E29");
            var Q24;
            Q24=sQuery(id+"F12.wireOp",EDGE,"E135");
            var Q25;
            Q25=sQuery(id+"F12.wireOp",EDGE,"E54");
            var Q26;
            Q26=sQuery(id+"F12.wireOp",EDGE,"E123");
            var Q27;
            Q27=sQuery(id+"F12.wireOp",EDGE,"E31");
            var Q28;
            Q28=sQuery(id+"F12.wireOp",EDGE,"E90");
            var Q29;
            Q29=sQuery(id+"F12.wireOp",EDGE,"E100");
            var Q30;
            Q30=sQuery(id+"F12.wireOp",EDGE,"E16");
            var Q31;
            Q31=sQuery(id+"F12.wireOp",EDGE,"E63");
            var Q32;
            Q32=sQuery(id+"F12.wireOp",EDGE,"E64");
            var Q33;
            Q33=sQuery(id+"F12.wireOp",EDGE,"E56");
            var Q34;
            Q34=sQuery(id+"F12.wireOp",EDGE,"E68");
            var Q35;
            Q35=sQuery(id+"F12.wireOp",EDGE,"E66");
            var Q36;
            Q36=sQuery(id+"F12.wireOp",EDGE,"E88");
            var Q37;
            Q37=sQuery(id+"F12.wireOp",EDGE,"E67");
            var Q38;
            Q38=sQuery(id+"F12.wireOp",EDGE,"E137");
            var Q39;
            Q39=sQuery(id+"F12.wireOp",EDGE,"E129");
            var Q40;
            Q40=sQuery(id+"F12.wireOp",EDGE,"E136");
            var Q41;
            Q41=sQuery(id+"F12.wireOp",EDGE,"E19");
            var Q42;
            Q42=sQuery(id+"F12.wireOp",EDGE,"E17");
            var Q43;
            Q43=sQuery(id+"F12.wireOp",EDGE,"E30");
            var Q44;
            Q44=sQuery(id+"F12.wireOp",EDGE,"E52");
            var Q45;
            Q45=sQuery(id+"F12.wireOp",EDGE,"E99");
            var Q46;
            Q46=sQuery(id+"F12.wireOp",EDGE,"E152");
            var Q47;
            Q47=sQuery(id+"F12.wireOp",EDGE,"E15");
            var Q48;
            Q48=sQuery(id+"F12.wireOp",EDGE,"E21");
            var Q49;
            Q49=sQuery(id+"F12.wireOp",EDGE,"E128");
            var Q50;
            Q50=sQuery(id+"F12.wireOp",EDGE,"E89");
            var Q51;
            Q51=sQuery(id+"F12.wireOp",EDGE,"E18");
            var Q52;
            Q52=sQuery(id+"F12.wireOp",EDGE,"E28");
            var Q53;
            Q53=sQuery(id+"F12.wireOp",EDGE,"E32");
            var Q54;
            Q54=sQuery(id+"F12.wireOp",EDGE,"E134");
            var Q55;
            Q55=sQuery(id+"F12.wireOp",EDGE,"E69");
            var Q56;
            Q56=sQuery(id+"F12.wireOp",EDGE,"E150");
            var Q57;
            Q57=sQuery(id+"F12.wireOp",EDGE,"E159");
            var Q58;
            Q58=sQuery(id+"F12.wireOp",EDGE,"E140");
            var Q59;
            Q59=sQuery(id+"F12.wireOp",EDGE,"E130");
            var Q60;
            Q60=sQuery(id+"F12.wireOp",EDGE,"E165");
            var Q61;
            Q61=sQuery(id+"F12.wireOp",EDGE,"E154");
            var Q62;
            Q62=sQuery(id+"F12.wireOp",EDGE,"E141");
            var Q63;
            Q63=sQuery(id+"F12.wireOp",EDGE,"E131");
            var Q64;
            Q64=sQuery(id+"F12.wireOp",EDGE,"E57");
            var Q65;
            Q65=sQuery(id+"F12.wireOp",EDGE,"E20");
            var Q66;
            Q66=sQuery(id+"F12.wireOp",EDGE,"E132");
            var Q67;
            Q67=sQuery(id+"F12.wireOp",EDGE,"E151");
            var Q68;
            Q68=sQuery(id+"F12.wireOp",EDGE,"E133");
            var Q69;
            Q69=sQuery(id+"F12.wireOp",EDGE,"E139");
            var Q70;
            Q70=sQuery(id+"F12.wireOp",EDGE,"E158");
            var Q71;
            Q71=sQuery(id+"F12.wireOp",EDGE,"E59");
            var Q72;
            Q72=sQuery(id+"F12.wireOp",EDGE,"E58");
            var Q73;
            Q73=sQuery(id+"F12.wireOp",EDGE,"E27");
            var Q74;
            Q74=sQuery(id+"F12.wireOp",EDGE,"E156");
            var Q75;
            Q75=sQuery(id+"F12.wireOp",EDGE,"E162");
            var Q76;
            Q76=sQuery(id+"F12.wireOp",EDGE,"E160");
            var Q77;
            Q77=sQuery(id+"F12.wireOp",EDGE,"E61");
            var Q78;
            Q78=sQuery(id+"F12.wireOp",EDGE,"E95");
            var Q79;
            Q79=sQuery(id+"F12.wireOp",EDGE,"E96");
            var Q80;
            Q80=sQuery(id+"F12.wireOp",EDGE,"E161");
            var Q81;
            Q81=sQuery(id+"F12.wireOp",EDGE,"E138");
            var Q82;
            Q82=sQuery(id+"F12.wireOp",EDGE,"E97");
            var Q83;
            Q83=sQuery(id+"F12.wireOp",EDGE,"E155");
            var Q84;
            Q84=sQuery(id+"F12.wireOp",EDGE,"E98");
            var Q85;
            Q85=sQuery(id+"F12.wireOp",EDGE,"E62");
            var Q86;
            Q86=sQuery(id+"F12.wireOp",EDGE,"E157");
            var Q87;
            Q87=sQuery(id+"F12.wireOp",EDGE,"E153");
            var Q88;
            Q88=sQuery(id+"F12.wireOp",EDGE,"E164");
            var Q89;
            Q89=sQuery(id+"F12.wireOp",EDGE,"E148");
            var Q90;
            Q90=sQuery(id+"F12.wireOp",EDGE,"E143");
            var Q91;
            Q91=sQuery(id+"F12.wireOp",EDGE,"E146");
            var Q92;
            Q92=sQuery(id+"F12.wireOp",EDGE,"E50");
            var Q93;
            Q93=sQuery(id+"F12.wireOp",EDGE,"E44");
            var Q94;
            Q94=sQuery(id+"F12.wireOp",EDGE,"E47");
            var Q95;
            Q95=sQuery(id+"F12.wireOp",EDGE,"E40");
            var Q96;
            Q96=sQuery(id+"F12.wireOp",EDGE,"E142");
            var Q97;
            Q97=sQuery(id+"F12.wireOp",EDGE,"E51");
            var Q98;
            Q98=sQuery(id+"F12.wireOp",EDGE,"E94");
            var Q99;
            Q99=sQuery(id+"F12.wireOp",EDGE,"E34");
            var Q100;
            Q100=sQuery(id+"F12.wireOp",EDGE,"E60");
            var Q101;
            Q101=sQuery(id+"F12.wireOp",EDGE,"E33");
            var Q102;
            Q102=sQuery(id+"F12.wireOp",EDGE,"E144");
            var Q103;
            Q103=sQuery(id+"F12.wireOp",EDGE,"E122");
            var Q104;
            Q104=sQuery(id+"F12.wireOp",EDGE,"E80");
            var Q105;
            Q105=sQuery(id+"F12.wireOp",EDGE,"E120");
            var Q106;
            Q106=sQuery(id+"F12.wireOp",EDGE,"E145");
            var Q107;
            Q107=sQuery(id+"F12.wireOp",EDGE,"E147");
            var Q108;
            Q108=sQuery(id+"F12.wireOp",EDGE,"E163");
            var Q109;
            Q109=sQuery(id+"F12.wireOp",EDGE,"E23");
            var Q110;
            Q110=sQuery(id+"F12.wireOp",EDGE,"E24");
            var Q111;
            Q111=sQuery(id+"F12.wireOp",EDGE,"E85");
            var Q112;
            Q112=sQuery(id+"F12.wireOp",EDGE,"E39");
            var Q113;
            Q113=sQuery(id+"F12.wireOp",EDGE,"E86");
            var Q114;
            Q114=sQuery(id+"F12.wireOp",EDGE,"E35");
            var Q115;
            Q115=sQuery(id+"F12.wireOp",EDGE,"E82");
            var Q116;
            Q116=sQuery(id+"F12.wireOp",EDGE,"E119");
            var Q117;
            Q117=sQuery(id+"F12.wireOp",EDGE,"E25");
            var Q118;
            Q118=sQuery(id+"F12.wireOp",EDGE,"E46");
            var Q119;
            Q119=sQuery(id+"F12.wireOp",EDGE,"E26");
            var Q120;
            Q120=sQuery(id+"F12.wireOp",EDGE,"E118");
            var Q121;
            Q121=sQuery(id+"F12.wireOp",EDGE,"E49");
            var Q122;
            Q122=sQuery(id+"F12.wireOp",EDGE,"E87");
            var Q123;
            Q123=sQuery(id+"F12.wireOp",EDGE,"E38");
            var Q124;
            Q124=sQuery(id+"F12.wireOp",EDGE,"E37");
            var Q125;
            Q125=sQuery(id+"F12.wireOp",EDGE,"E70");
            var Q126;
            Q126=sQuery(id+"F12.wireOp",EDGE,"E72");
            var Q127;
            Q127=sQuery(id+"F12.wireOp",EDGE,"E22");
            var Q128;
            Q128=sQuery(id+"F12.wireOp",EDGE,"E36");
            var Q129;
            Q129=sQuery(id+"F12.wireOp",EDGE,"E48");
            var Q130;
            Q130=sQuery(id+"F12.wireOp",EDGE,"E121");
            var Q131;
            Q131=sQuery(id+"F12.wireOp",EDGE,"E116");
            var Q132;
            Q132=sQuery(id+"F12.wireOp",EDGE,"E81");
            var Q133;
            Q133=sQuery(id+"F12.wireOp",EDGE,"E45");
            var Q134;
            Q134=sQuery(id+"F12.wireOp",EDGE,"E84");
            var Q135;
            Q135=sQuery(id+"F12.wireOp",EDGE,"E71");
            var Q136;
            Q136=sQuery(id+"F12.wireOp",EDGE,"E76");
            var Q137;
            Q137=sQuery(id+"F12.wireOp",EDGE,"E14");
            var Q138;
            Q138=sQuery(id+"F12.wireOp",EDGE,"E105");
            var Q139;
            Q139=sQuery(id+"F12.wireOp",EDGE,"E108");
            var Q140;
            Q140=sQuery(id+"F12.wireOp",EDGE,"E13");
            var Q141;
            Q141=sQuery(id+"F12.wireOp",EDGE,"E11");
            var Q142;
            Q142=sQuery(id+"F12.wireOp",EDGE,"E8");
            var Q143;
            Q143=sQuery(id+"F12.wireOp",EDGE,"E110");
            var Q144;
            Q144=sQuery(id+"F12.wireOp",EDGE,"E83");
            var Q145;
            Q145=sQuery(id+"F12.wireOp",EDGE,"E111");
            var Q146;
            Q146=sQuery(id+"F12.wireOp",EDGE,"E107");
            var Q147;
            Q147=sQuery(id+"F12.wireOp",EDGE,"E73");
            var Q148;
            Q148=sQuery(id+"F12.wireOp",EDGE,"E106");
            var Q149;
            Q149=sQuery(id+"F12.wireOp",EDGE,"E117");
            var Q150;
            Q150=sQuery(id+"F12.wireOp",EDGE,"E75");
            var Q151;
            Q151=sQuery(id+"F12.wireOp",EDGE,"E74");
            var Q152;
            Q152=sQuery(id+"F12.wireOp",EDGE,"E12");
            var Q153;
            Q153=sQuery(id+"F12.wireOp",EDGE,"E10");
            var Q154;
            Q154=sQuery(id+"F12.wireOp",EDGE,"E112");
            var Q155;
            Q155=sQuery(id+"F12.wireOp",EDGE,"E109");
            var Q156;
            Q156=sQuery(id+"F12.wireOp",EDGE,"E9");
            extrude(context, id + "F13", {"entities" : qUnion([Q0]), "surfaceEntities" : qUnion([Q1, Q2, Q3, Q4, Q5, Q6, Q7, Q8, Q9, Q10, Q11, Q12, Q13, Q14, Q15, Q16, Q17, Q18, Q19, Q20, Q21, Q22, Q23, Q24, Q25, Q26, Q27, Q28, Q29, Q30, Q31, Q32, Q33, Q34, Q35, Q36, Q37, Q38, Q39, Q40, Q41, Q42, Q43, Q44, Q45, Q46, Q47, Q48, Q49, Q50, Q51, Q52, Q53, Q54, Q55, Q56, Q57, Q58, Q59, Q60, Q61, Q62, Q63, Q64, Q65, Q66, Q67, Q68, Q69, Q70, Q71, Q72, Q73, Q74, Q75, Q76, Q77, Q78, Q79, Q80, Q81, Q82, Q83, Q84, Q85, Q86, Q87, Q88, Q89, Q90, Q91, Q92, Q93, Q94, Q95, Q96, Q97, Q98, Q99, Q100, Q101, Q102, Q103, Q104, Q105, Q106, Q107, Q108, Q109, Q110, Q111, Q112, Q113, Q114, Q115, Q116, Q117, Q118, Q119, Q120, Q121, Q122, Q123, Q124, Q125, Q126, Q127, Q128, Q129, Q130, Q131, Q132, Q133, Q134, Q135, Q136, Q137, Q138, Q139, Q140, Q141, Q142, Q143, Q144, Q145, Q146, Q147, Q148, Q149, Q150, Q151, Q152, Q153, Q154, Q155, Q156]), "depth" : 1600 * mm, "offsetDistance" : 25 * mm, "hasSecondDirection" : true, "secondDirectionOppositeDirection" : true, "secondDirectionDepth" : 100 * mm});
        }
        {
            var Q0;
            Q0=makeQuery(id+"F13.opExtrude","SWEPT_BODY",BODY,{"disambiguationData":[OSD([sQuery(id+"F12.wireOp",EDGE,"E163")])]});
            var Q1;
            Q1=makeQuery(id+"F13.opExtrude","SWEPT_BODY",BODY,{"disambiguationData":[OSD([sQuery(id+"F12.wireOp",EDGE,"E55")])]});
            transform(context, id + "F14", {"entities" : qUnion([Q0, Q1]), "transformType" : TransformType.TRANSLATION_3D, "dx" : 0 * mm, "dy" : 0 * mm, "dz" : -350 * mm, "makeCopy" : true});
        }
        {
            var Q0;
            Q0=makeQuery(id+"F14.opPattern","COPY",BODY,{"derivedFrom":makeQuery(id+"F13.opExtrude","SWEPT_BODY",BODY,{"disambiguationData":[OSD([sQuery(id+"F12.wireOp",EDGE,"E55")])]}),"instanceName":"1"});
            var Q1;
            Q1=makeQuery(id+"F14.opPattern","COPY",BODY,{"derivedFrom":makeQuery(id+"F13.opExtrude","SWEPT_BODY",BODY,{"disambiguationData":[OSD([sQuery(id+"F12.wireOp",EDGE,"E163")])]}),"instanceName":"1"});
            var Q2;
            Q2=makeQuery(id+"F13.opExtrude","SWEPT_BODY",BODY,{"disambiguationData":[OSD([sQuery(id+"F12.wireOp",EDGE,"E163")])]});
            var Q3;
            Q3=makeQuery(id+"F13.opExtrude","SWEPT_BODY",BODY,{"disambiguationData":[OSD([sQuery(id+"F12.wireOp",EDGE,"E55")])]});
            transform(context, id + "F15", {"entities" : qUnion([Q0, Q1, Q2, Q3]), "transformType" : TransformType.TRANSLATION_3D, "dx" : 0 * mm, "dy" : 20 * mm, "dz" : 0 * mm, "makeCopy" : false});
        }
    });
